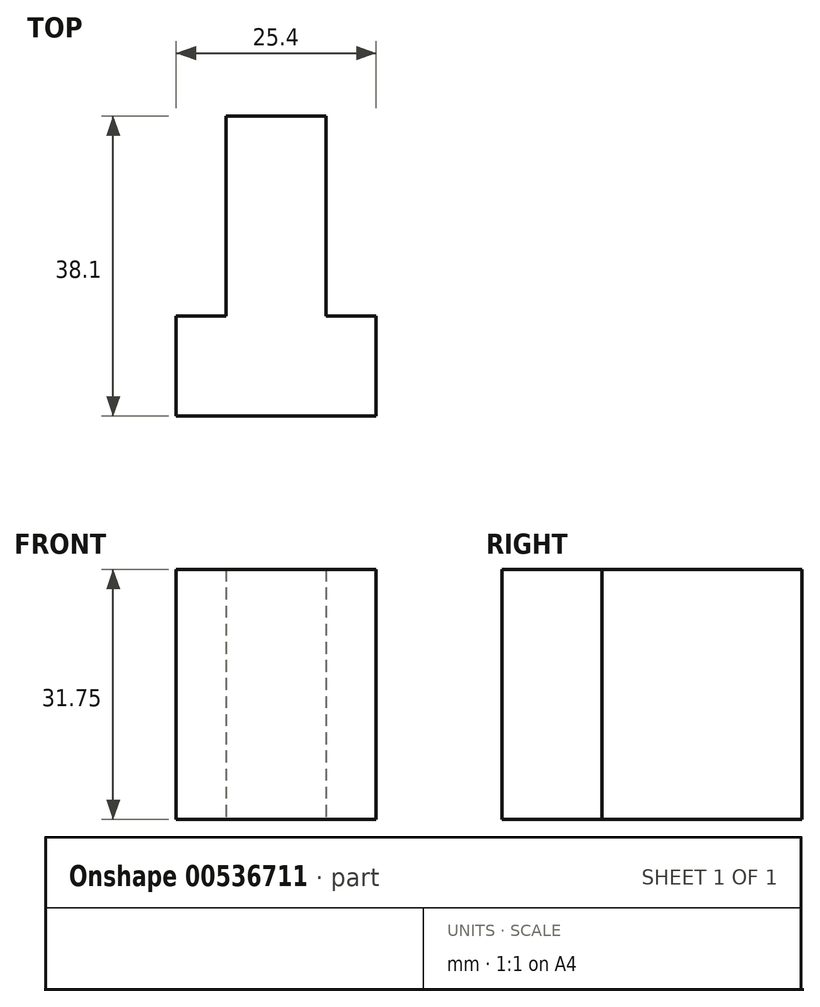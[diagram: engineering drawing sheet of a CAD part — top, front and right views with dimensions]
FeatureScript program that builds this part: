
annotation { "Feature Type Name" : "Feature", "Feature Type Description" : "" }
export const myFeature = defineFeature(function(context is Context, id is Id, definition is map)
    precondition{}
    {
        {
            var Q0;
            Q0=qCreatedBy(makeId("Top.planeOp"),FACE);
            var sketch = newSketch(context, id + "F0", { "sketchPlane" : qUnion([Q0])});
            skLineSegment(sketch, "E0", {"start": v(0, 0) * mm, "end": v(0, 25.4) * mm});
            skLineSegment(sketch, "E1", {"start": v(0, 25.4) * mm, "end": v(12.7, 25.4) * mm});
            skLineSegment(sketch, "E2", {"start": v(12.7, 25.4) * mm, "end": v(12.7, 0) * mm});
            skLineSegment(sketch, "E3", {"start": v(12.7, 0) * mm, "end": v(19.05, 0) * mm});
            skLineSegment(sketch, "E4", {"start": v(19.05, 0) * mm, "end": v(19.05, -12.7) * mm});
            skLineSegment(sketch, "E5", {"start": v(0, 0) * mm, "end": v(-6.35, 0) * mm});
            skLineSegment(sketch, "E6", {"start": v(-6.35, 0) * mm, "end": v(-6.35, -12.7) * mm});
            skLineSegment(sketch, "E7", {"start": v(-6.35, -12.7) * mm, "end": v(19.05, -12.7) * mm});
            skSolve(sketch);
        }
        {
            var Q0;
            Q0 = qSketchRegion(id + "F0", true);
            extrude(context, id + "F1", {"entities" : qUnion([Q0]), "depth" : 31.75 * mm, "offsetDistance" : 25.4 * mm});
        }
    });
